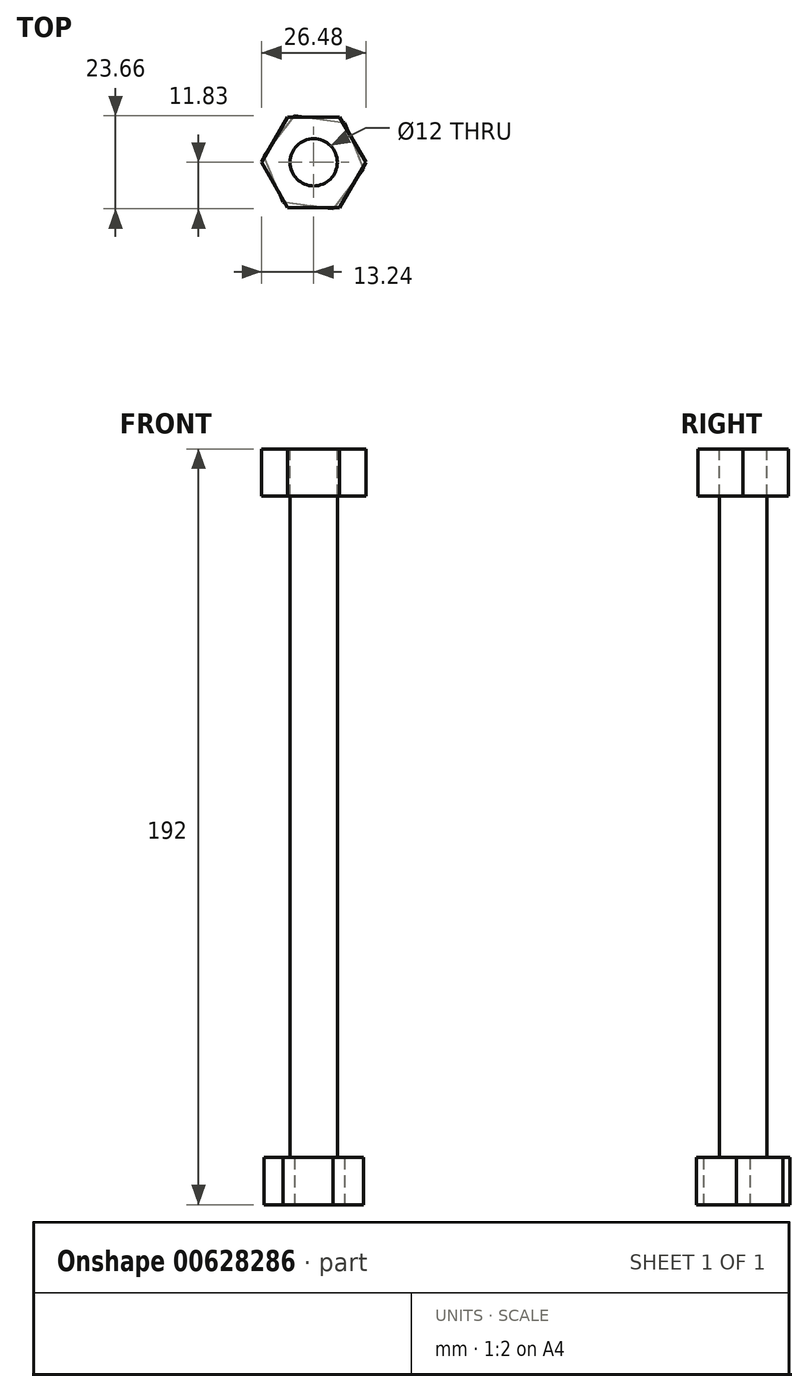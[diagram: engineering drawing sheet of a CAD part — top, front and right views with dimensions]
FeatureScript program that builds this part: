
annotation { "Feature Type Name" : "Feature", "Feature Type Description" : "" }
export const myFeature = defineFeature(function(context is Context, id is Id, definition is map)
    precondition{}
    {
        {
            var Q0;
            Q0=qCreatedBy(makeId("Top.planeOp"),FACE);
            var sketch = newSketch(context, id + "F0", { "sketchPlane" : qUnion([Q0])});
            skCircle(sketch, "E0", {"center": v(0, 0) * mm, "radius": 6 * mm});
            skCircle(sketch, "E1.cCircle", {"center": v(0, 0) * mm, "radius": 11.08 * mm, "construction": true});
            skLineSegment(sketch, "E1.0", {"start": v(-12.68, 1.69) * mm, "end": v(-4.88, 11.83) * mm});
            skLineSegment(sketch, "E1.1", {"start": v(-4.88, 11.83) * mm, "end": v(7.8, 10.14) * mm});
            skLineSegment(sketch, "E1.2", {"start": v(7.8, 10.14) * mm, "end": v(12.68, -1.69) * mm});
            skLineSegment(sketch, "E1.3", {"start": v(12.68, -1.69) * mm, "end": v(4.88, -11.83) * mm});
            skLineSegment(sketch, "E1.4", {"start": v(4.88, -11.83) * mm, "end": v(-7.8, -10.14) * mm});
            skLineSegment(sketch, "E1.5", {"start": v(-7.8, -10.14) * mm, "end": v(-12.68, 1.69) * mm});
            skPoint(sketch, "E1.0.midPoint", {"position": v(-8.78, 6.76) * mm});
            skSolve(sketch);
        }
        {
            var Q0;
            Q0=makeQuery(id+"F0.imprint","IMPRINT",FACE,{"disambiguationData":[TD([[makeQuery(id+"F0.imprint","IMPRINT",EDGE,{"derivedFrom":sQuery(id+"F0.wireOp",EDGE,"E0")}),1.0]])]});
            extrude(context, id + "F1", {"entities" : qUnion([Q0]), "depth" : 192 * mm, "offsetDistance" : 25 * mm});
        }
        {
            var Q0;
            Q0 = qSketchRegion(id + "F0", true);
            extrude(context, id + "F2", {"entities" : qUnion([Q0]), "operationType" : NewBodyOperationType.ADD, "depth" : 12 * mm, "offsetDistance" : 25 * mm});
        }
        {
            var Q0;
            Q0=makeQuery(id+"F1.opExtrude","CAP_FACE",FACE,{"disambiguationData":[OSD([sQuery(id+"F0.wireOp",EDGE,"E0")])],"isStart":false});
            var sketch = newSketch(context, id + "F3", { "sketchPlane" : qUnion([Q0])});
            skCircle(sketch, "E2.cCircle", {"center": v(0, 0) * mm, "radius": 11.47 * mm, "construction": true});
            skLineSegment(sketch, "E2.0", {"start": v(6.62, -11.47) * mm, "end": v(-6.62, -11.47) * mm});
            skLineSegment(sketch, "E2.1", {"start": v(-6.62, -11.47) * mm, "end": v(-13.24, 0) * mm});
            skLineSegment(sketch, "E2.2", {"start": v(-13.24, 0) * mm, "end": v(-6.62, 11.47) * mm});
            skLineSegment(sketch, "E2.3", {"start": v(-6.62, 11.47) * mm, "end": v(6.62, 11.47) * mm});
            skLineSegment(sketch, "E2.4", {"start": v(6.62, 11.47) * mm, "end": v(13.24, 0) * mm});
            skLineSegment(sketch, "E2.5", {"start": v(13.24, 0) * mm, "end": v(6.62, -11.47) * mm});
            skPoint(sketch, "E2.0.midPoint", {"position": v(0, -11.47) * mm});
            skSolve(sketch);
        }
        {
            var Q0;
            Q0=makeQuery(id+"F3.imprint","IMPRINT",FACE,{"disambiguationData":[TD([[makeQuery(id+"F3.imprint","IMPRINT",EDGE,{"derivedFrom":sQuery(id+"F3.wireOp",EDGE,"E2.0")}),-1.0]])]});
            extrude(context, id + "F4", {"entities" : qUnion([Q0]), "oppositeDirection" : true, "depth" : 12 * mm, "offsetDistance" : 25 * mm});
        }
    });
